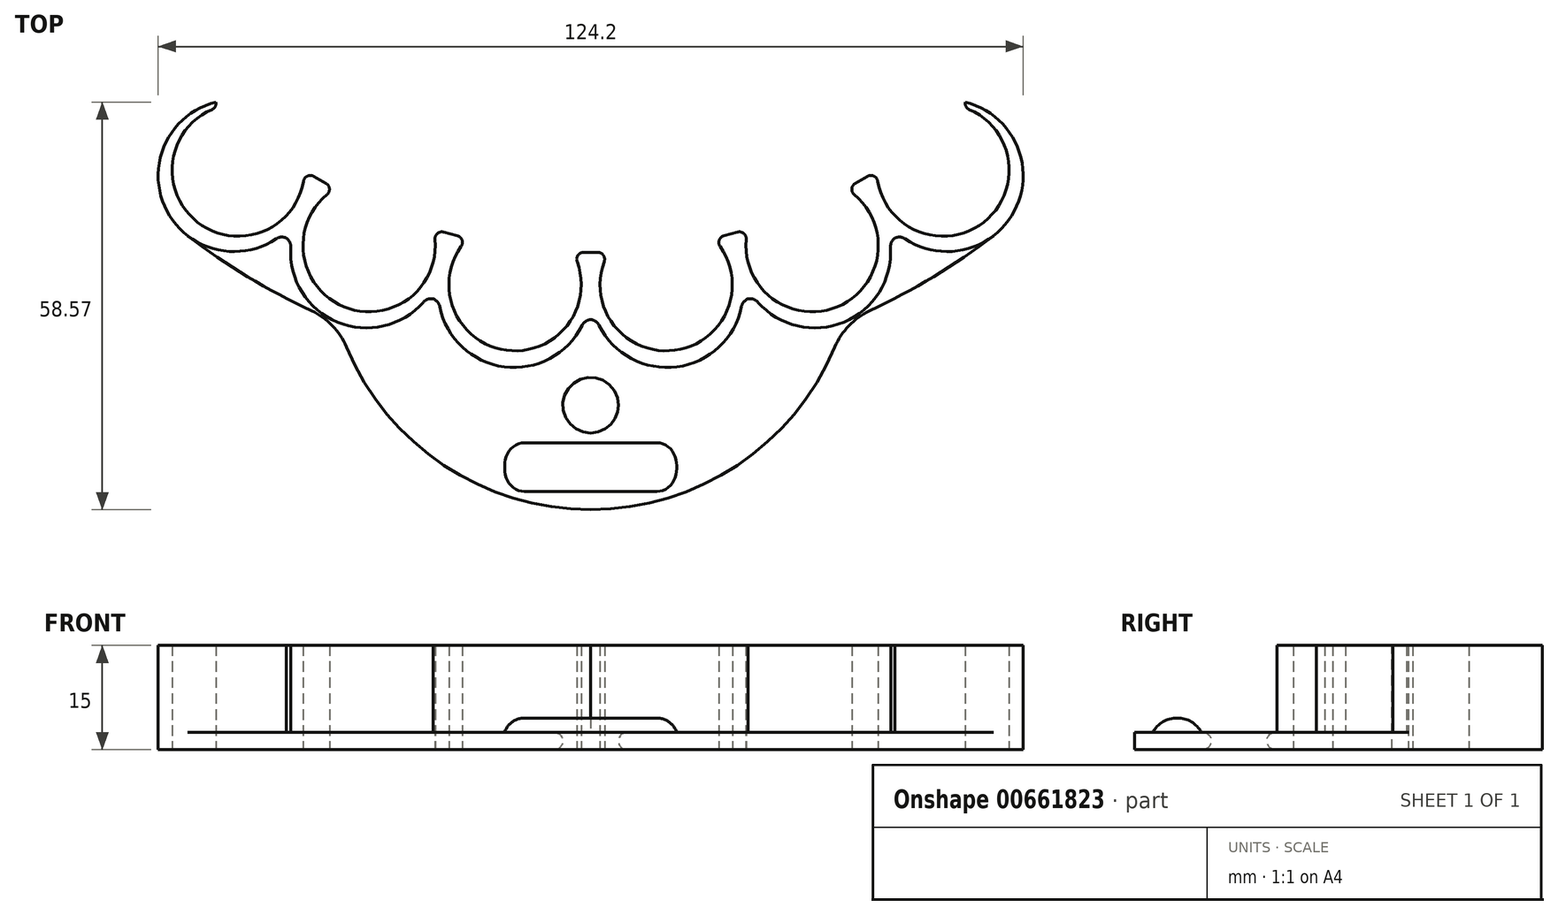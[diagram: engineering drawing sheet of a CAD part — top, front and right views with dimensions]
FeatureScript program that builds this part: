
annotation { "Feature Type Name" : "Feature", "Feature Type Description" : "" }
export const myFeature = defineFeature(function(context is Context, id is Id, definition is map)
    precondition{}
    {
        {
            assignVariable(context, id + "F0", {"name" : "clipHeight", "anyValue" : 15 * mm});
        }
        {
            var Q0;
            Q0=qCreatedBy(makeId("Top.planeOp"),FACE);
            var sketch = newSketch(context, id + "F1", { "sketchPlane" : qUnion([Q0])});
            skCircle(sketch, "E0", {"center": v(0, 0) * mm, "radius": 9.5 * mm});
            skCircle(sketch, "E1", {"center": v(0, 0) * mm, "radius": 10.3 * mm});
            skLineSegment(sketch, "E2", {"start": v(0, 0) * mm, "end": v(0, 25.39) * mm, "construction": true});
            skLineSegment(sketch, "E3", {"start": v(0, 0) * mm, "end": v(-8.5, 5.82) * mm});
            skLineSegment(sketch, "E4.MirrorCS", {"start": v(0, 0) * mm, "end": v(8.5, 5.82) * mm});
            skLineSegment(sketch, "E5", {"start": v(0, -10.3) * mm, "end": v(0, -11.9) * mm, "construction": true});
            skArc(sketch, "E6", {"start": v(-8.5, 5.82) * mm, "mid": v(0, -11.9) * mm, "end": v(8.5, 5.82) * mm});
            skLineSegment(sketch, "E7", {"start": v(0, -11.9) * mm, "end": v(0, 83.1) * mm, "construction": true});
            skLineSegment(sketch, "E8.1.0", {"start": v(24.59, -8.66) * mm, "end": v(0, 83.1) * mm, "construction": true});
            skArc(sketch, "E8.1.1", {"start": v(11.8, 6.25) * mm, "mid": v(24.59, -8.66) * mm, "end": v(28.21, 10.65) * mm});
            skCircle(sketch, "E8.1.2", {"center": v(21.5, 2.83) * mm, "radius": 10.3 * mm});
            skCircle(sketch, "E8.1.3", {"center": v(21.5, 2.83) * mm, "radius": 9.5 * mm});
            skLineSegment(sketch, "E8.1.4", {"start": v(21.5, 2.83) * mm, "end": v(14.94, 27.36) * mm, "construction": true});
            skLineSegment(sketch, "E8.1.5", {"start": v(24.17, -7.12) * mm, "end": v(24.59, -8.66) * mm, "construction": true});
            skLineSegment(sketch, "E8.1.6", {"start": v(21.5, 2.83) * mm, "end": v(28.21, 10.65) * mm});
            skLineSegment(sketch, "E8.1.7", {"start": v(21.5, 2.83) * mm, "end": v(11.8, 6.25) * mm});
            skLineSegment(sketch, "E8.2.0", {"start": v(47.5, 0.83) * mm, "end": v(0, 83.1) * mm, "construction": true});
            skArc(sketch, "E8.2.1", {"start": v(31.28, 11.92) * mm, "mid": v(47.5, 0.83) * mm, "end": v(46, 20.42) * mm});
            skCircle(sketch, "E8.2.2", {"center": v(41.55, 11.13) * mm, "radius": 10.3 * mm});
            skCircle(sketch, "E8.2.3", {"center": v(41.55, 11.13) * mm, "radius": 9.5 * mm});
            skLineSegment(sketch, "E8.2.4", {"start": v(41.55, 11.13) * mm, "end": v(28.86, 33.12) * mm, "construction": true});
            skLineSegment(sketch, "E8.2.5", {"start": v(46.7, 2.21) * mm, "end": v(47.5, 0.83) * mm, "construction": true});
            skLineSegment(sketch, "E8.2.6", {"start": v(41.55, 11.13) * mm, "end": v(46, 20.42) * mm});
            skLineSegment(sketch, "E8.2.7", {"start": v(41.55, 11.13) * mm, "end": v(31.28, 11.92) * mm});
            skLineSegment(sketch, "E8.3.0", {"start": v(67.18, 15.92) * mm, "end": v(0, 83.1) * mm, "construction": true});
            skArc(sketch, "E8.3.1", {"start": v(48.64, 22.44) * mm, "mid": v(67.18, 15.92) * mm, "end": v(60.66, 34.46) * mm});
            skCircle(sketch, "E8.3.2", {"center": v(58.76, 24.34) * mm, "radius": 10.3 * mm});
            skCircle(sketch, "E8.3.3", {"center": v(58.76, 24.34) * mm, "radius": 9.5 * mm});
            skLineSegment(sketch, "E8.3.4", {"start": v(58.76, 24.34) * mm, "end": v(40.8, 42.3) * mm, "construction": true});
            skLineSegment(sketch, "E8.3.5", {"start": v(66.04, 17.06) * mm, "end": v(67.18, 15.92) * mm, "construction": true});
            skLineSegment(sketch, "E8.3.6", {"start": v(58.76, 24.34) * mm, "end": v(60.66, 34.46) * mm});
            skLineSegment(sketch, "E8.3.7", {"start": v(58.76, 24.34) * mm, "end": v(48.64, 22.44) * mm});
            skLineSegment(sketch, "E8.4.0", {"start": v(82.27, 35.6) * mm, "end": v(0, 83.1) * mm, "construction": true});
            skArc(sketch, "E8.4.1", {"start": v(62.68, 37.1) * mm, "mid": v(82.27, 35.6) * mm, "end": v(71.18, 51.82) * mm});
            skCircle(sketch, "E8.4.2", {"center": v(71.97, 41.55) * mm, "radius": 10.3 * mm});
            skCircle(sketch, "E8.4.3", {"center": v(71.97, 41.55) * mm, "radius": 9.5 * mm});
            skLineSegment(sketch, "E8.4.4", {"start": v(71.97, 41.55) * mm, "end": v(49.98, 54.24) * mm, "construction": true});
            skLineSegment(sketch, "E8.4.5", {"start": v(80.89, 36.4) * mm, "end": v(82.27, 35.6) * mm, "construction": true});
            skLineSegment(sketch, "E8.4.6", {"start": v(71.97, 41.55) * mm, "end": v(71.18, 51.82) * mm});
            skLineSegment(sketch, "E8.4.7", {"start": v(71.97, 41.55) * mm, "end": v(62.68, 37.1) * mm});
            skLineSegment(sketch, "E8.5.0", {"start": v(91.76, 58.51) * mm, "end": v(0, 83.1) * mm, "construction": true});
            skArc(sketch, "E8.5.1", {"start": v(72.45, 54.89) * mm, "mid": v(91.76, 58.51) * mm, "end": v(76.85, 71.3) * mm});
            skCircle(sketch, "E8.5.2", {"center": v(80.27, 61.6) * mm, "radius": 10.3 * mm});
            skCircle(sketch, "E8.5.3", {"center": v(80.27, 61.6) * mm, "radius": 9.5 * mm});
            skLineSegment(sketch, "E8.5.4", {"start": v(80.27, 61.6) * mm, "end": v(55.74, 68.16) * mm, "construction": true});
            skLineSegment(sketch, "E8.5.5", {"start": v(90.22, 58.93) * mm, "end": v(91.76, 58.51) * mm, "construction": true});
            skLineSegment(sketch, "E8.5.6", {"start": v(80.27, 61.6) * mm, "end": v(76.85, 71.3) * mm});
            skLineSegment(sketch, "E8.5.7", {"start": v(80.27, 61.6) * mm, "end": v(72.45, 54.89) * mm});
            skLineSegment(sketch, "E8.6.0", {"start": v(95, 83.1) * mm, "end": v(0, 83.1) * mm, "construction": true});
            skArc(sketch, "E8.6.1", {"start": v(77.28, 74.6) * mm, "mid": v(95, 83.1) * mm, "end": v(77.28, 91.6) * mm});
            skCircle(sketch, "E8.6.2", {"center": v(83.1, 83.1) * mm, "radius": 10.3 * mm});
            skCircle(sketch, "E8.6.3", {"center": v(83.1, 83.1) * mm, "radius": 9.5 * mm});
            skLineSegment(sketch, "E8.6.4", {"start": v(83.1, 83.1) * mm, "end": v(57.71, 83.1) * mm, "construction": true});
            skLineSegment(sketch, "E8.6.5", {"start": v(93.4, 83.1) * mm, "end": v(95, 83.1) * mm, "construction": true});
            skLineSegment(sketch, "E8.6.6", {"start": v(83.1, 83.1) * mm, "end": v(77.28, 91.6) * mm});
            skLineSegment(sketch, "E8.6.7", {"start": v(83.1, 83.1) * mm, "end": v(77.28, 74.6) * mm});
            skLineSegment(sketch, "E8.7.0", {"start": v(91.76, 107.69) * mm, "end": v(0, 83.1) * mm, "construction": true});
            skArc(sketch, "E8.7.1", {"start": v(76.85, 94.9) * mm, "mid": v(91.76, 107.69) * mm, "end": v(72.45, 111.31) * mm});
            skCircle(sketch, "E8.7.2", {"center": v(80.27, 104.6) * mm, "radius": 10.3 * mm});
            skCircle(sketch, "E8.7.3", {"center": v(80.27, 104.6) * mm, "radius": 9.5 * mm});
            skLineSegment(sketch, "E8.7.4", {"start": v(80.27, 104.6) * mm, "end": v(55.74, 98.04) * mm, "construction": true});
            skLineSegment(sketch, "E8.7.5", {"start": v(90.22, 107.27) * mm, "end": v(91.76, 107.69) * mm, "construction": true});
            skLineSegment(sketch, "E8.7.6", {"start": v(80.27, 104.6) * mm, "end": v(72.45, 111.31) * mm});
            skLineSegment(sketch, "E8.7.7", {"start": v(80.27, 104.6) * mm, "end": v(76.85, 94.9) * mm});
            skLineSegment(sketch, "E8.8.0", {"start": v(82.27, 130.6) * mm, "end": v(0, 83.1) * mm, "construction": true});
            skArc(sketch, "E8.8.1", {"start": v(71.18, 114.38) * mm, "mid": v(82.27, 130.6) * mm, "end": v(62.68, 129.1) * mm});
            skCircle(sketch, "E8.8.2", {"center": v(71.97, 124.65) * mm, "radius": 10.3 * mm});
            skCircle(sketch, "E8.8.3", {"center": v(71.97, 124.65) * mm, "radius": 9.5 * mm});
            skLineSegment(sketch, "E8.8.4", {"start": v(71.97, 124.65) * mm, "end": v(49.98, 111.96) * mm, "construction": true});
            skLineSegment(sketch, "E8.8.5", {"start": v(80.89, 129.8) * mm, "end": v(82.27, 130.6) * mm, "construction": true});
            skLineSegment(sketch, "E8.8.6", {"start": v(71.97, 124.65) * mm, "end": v(62.68, 129.1) * mm});
            skLineSegment(sketch, "E8.8.7", {"start": v(71.97, 124.65) * mm, "end": v(71.18, 114.38) * mm});
            skLineSegment(sketch, "E8.9.0", {"start": v(67.18, 150.28) * mm, "end": v(0, 83.1) * mm, "construction": true});
            skArc(sketch, "E8.9.1", {"start": v(60.66, 131.74) * mm, "mid": v(67.18, 150.28) * mm, "end": v(48.64, 143.76) * mm});
            skCircle(sketch, "E8.9.2", {"center": v(58.76, 141.86) * mm, "radius": 10.3 * mm});
            skCircle(sketch, "E8.9.3", {"center": v(58.76, 141.86) * mm, "radius": 9.5 * mm});
            skLineSegment(sketch, "E8.9.4", {"start": v(58.76, 141.86) * mm, "end": v(40.8, 123.9) * mm, "construction": true});
            skLineSegment(sketch, "E8.9.5", {"start": v(66.04, 149.14) * mm, "end": v(67.18, 150.28) * mm, "construction": true});
            skLineSegment(sketch, "E8.9.6", {"start": v(58.76, 141.86) * mm, "end": v(48.64, 143.76) * mm});
            skLineSegment(sketch, "E8.9.7", {"start": v(58.76, 141.86) * mm, "end": v(60.66, 131.74) * mm});
            skLineSegment(sketch, "E8.10.0", {"start": v(47.5, 165.37) * mm, "end": v(0, 83.1) * mm, "construction": true});
            skArc(sketch, "E8.10.1", {"start": v(46, 145.78) * mm, "mid": v(47.5, 165.37) * mm, "end": v(31.28, 154.28) * mm});
            skCircle(sketch, "E8.10.2", {"center": v(41.55, 155.07) * mm, "radius": 10.3 * mm});
            skCircle(sketch, "E8.10.3", {"center": v(41.55, 155.07) * mm, "radius": 9.5 * mm});
            skLineSegment(sketch, "E8.10.4", {"start": v(41.55, 155.07) * mm, "end": v(28.86, 133.08) * mm, "construction": true});
            skLineSegment(sketch, "E8.10.5", {"start": v(46.7, 163.99) * mm, "end": v(47.5, 165.37) * mm, "construction": true});
            skLineSegment(sketch, "E8.10.6", {"start": v(41.55, 155.07) * mm, "end": v(31.28, 154.28) * mm});
            skLineSegment(sketch, "E8.10.7", {"start": v(41.55, 155.07) * mm, "end": v(46, 145.78) * mm});
            skLineSegment(sketch, "E8.11.0", {"start": v(24.59, 174.86) * mm, "end": v(0, 83.1) * mm, "construction": true});
            skArc(sketch, "E8.11.1", {"start": v(28.21, 155.55) * mm, "mid": v(24.59, 174.86) * mm, "end": v(11.8, 159.95) * mm});
            skCircle(sketch, "E8.11.2", {"center": v(21.5, 163.37) * mm, "radius": 10.3 * mm});
            skCircle(sketch, "E8.11.3", {"center": v(21.5, 163.37) * mm, "radius": 9.5 * mm});
            skLineSegment(sketch, "E8.11.4", {"start": v(21.5, 163.37) * mm, "end": v(14.94, 138.84) * mm, "construction": true});
            skLineSegment(sketch, "E8.11.5", {"start": v(24.17, 173.32) * mm, "end": v(24.59, 174.86) * mm, "construction": true});
            skLineSegment(sketch, "E8.11.6", {"start": v(21.5, 163.37) * mm, "end": v(11.8, 159.95) * mm});
            skLineSegment(sketch, "E8.11.7", {"start": v(21.5, 163.37) * mm, "end": v(28.21, 155.55) * mm});
            skLineSegment(sketch, "E8.12.0", {"start": v(0, 178.1) * mm, "end": v(0, 83.1) * mm, "construction": true});
            skArc(sketch, "E8.12.1", {"start": v(8.5, 160.38) * mm, "mid": v(0, 178.1) * mm, "end": v(-8.5, 160.38) * mm});
            skCircle(sketch, "E8.12.2", {"center": v(0, 166.2) * mm, "radius": 10.3 * mm});
            skCircle(sketch, "E8.12.3", {"center": v(0, 166.2) * mm, "radius": 9.5 * mm});
            skLineSegment(sketch, "E8.12.4", {"start": v(0, 166.2) * mm, "end": v(0, 140.81) * mm, "construction": true});
            skLineSegment(sketch, "E8.12.5", {"start": v(0, 176.5) * mm, "end": v(0, 178.1) * mm, "construction": true});
            skLineSegment(sketch, "E8.12.6", {"start": v(0, 166.2) * mm, "end": v(-8.5, 160.38) * mm});
            skLineSegment(sketch, "E8.12.7", {"start": v(0, 166.2) * mm, "end": v(8.5, 160.38) * mm});
            skLineSegment(sketch, "E8.13.0", {"start": v(-24.59, 174.86) * mm, "end": v(0, 83.1) * mm, "construction": true});
            skArc(sketch, "E8.13.1", {"start": v(-11.8, 159.95) * mm, "mid": v(-24.59, 174.86) * mm, "end": v(-28.21, 155.55) * mm});
            skCircle(sketch, "E8.13.2", {"center": v(-21.5, 163.37) * mm, "radius": 10.3 * mm});
            skCircle(sketch, "E8.13.3", {"center": v(-21.5, 163.37) * mm, "radius": 9.5 * mm});
            skLineSegment(sketch, "E8.13.4", {"start": v(-21.5, 163.37) * mm, "end": v(-14.94, 138.84) * mm, "construction": true});
            skLineSegment(sketch, "E8.13.5", {"start": v(-24.17, 173.32) * mm, "end": v(-24.59, 174.86) * mm, "construction": true});
            skLineSegment(sketch, "E8.13.6", {"start": v(-21.5, 163.37) * mm, "end": v(-28.21, 155.55) * mm});
            skLineSegment(sketch, "E8.13.7", {"start": v(-21.5, 163.37) * mm, "end": v(-11.8, 159.95) * mm});
            skLineSegment(sketch, "E8.14.0", {"start": v(-47.5, 165.37) * mm, "end": v(0, 83.1) * mm, "construction": true});
            skArc(sketch, "E8.14.1", {"start": v(-31.28, 154.28) * mm, "mid": v(-47.5, 165.37) * mm, "end": v(-46, 145.78) * mm});
            skCircle(sketch, "E8.14.2", {"center": v(-41.55, 155.07) * mm, "radius": 10.3 * mm});
            skCircle(sketch, "E8.14.3", {"center": v(-41.55, 155.07) * mm, "radius": 9.5 * mm});
            skLineSegment(sketch, "E8.14.4", {"start": v(-41.55, 155.07) * mm, "end": v(-28.86, 133.08) * mm, "construction": true});
            skLineSegment(sketch, "E8.14.5", {"start": v(-46.7, 163.99) * mm, "end": v(-47.5, 165.37) * mm, "construction": true});
            skLineSegment(sketch, "E8.14.6", {"start": v(-41.55, 155.07) * mm, "end": v(-46, 145.78) * mm});
            skLineSegment(sketch, "E8.14.7", {"start": v(-41.55, 155.07) * mm, "end": v(-31.28, 154.28) * mm});
            skLineSegment(sketch, "E8.15.0", {"start": v(-67.18, 150.28) * mm, "end": v(0, 83.1) * mm, "construction": true});
            skArc(sketch, "E8.15.1", {"start": v(-48.64, 143.76) * mm, "mid": v(-67.18, 150.28) * mm, "end": v(-60.66, 131.74) * mm});
            skCircle(sketch, "E8.15.2", {"center": v(-58.76, 141.86) * mm, "radius": 10.3 * mm});
            skCircle(sketch, "E8.15.3", {"center": v(-58.76, 141.86) * mm, "radius": 9.5 * mm});
            skLineSegment(sketch, "E8.15.4", {"start": v(-58.76, 141.86) * mm, "end": v(-40.8, 123.9) * mm, "construction": true});
            skLineSegment(sketch, "E8.15.5", {"start": v(-66.04, 149.14) * mm, "end": v(-67.18, 150.28) * mm, "construction": true});
            skLineSegment(sketch, "E8.15.6", {"start": v(-58.76, 141.86) * mm, "end": v(-60.66, 131.74) * mm});
            skLineSegment(sketch, "E8.15.7", {"start": v(-58.76, 141.86) * mm, "end": v(-48.64, 143.76) * mm});
            skLineSegment(sketch, "E8.16.0", {"start": v(-82.27, 130.6) * mm, "end": v(0, 83.1) * mm, "construction": true});
            skArc(sketch, "E8.16.1", {"start": v(-62.68, 129.1) * mm, "mid": v(-82.27, 130.6) * mm, "end": v(-71.18, 114.38) * mm});
            skCircle(sketch, "E8.16.2", {"center": v(-71.97, 124.65) * mm, "radius": 10.3 * mm});
            skCircle(sketch, "E8.16.3", {"center": v(-71.97, 124.65) * mm, "radius": 9.5 * mm});
            skLineSegment(sketch, "E8.16.4", {"start": v(-71.97, 124.65) * mm, "end": v(-49.98, 111.96) * mm, "construction": true});
            skLineSegment(sketch, "E8.16.5", {"start": v(-80.89, 129.8) * mm, "end": v(-82.27, 130.6) * mm, "construction": true});
            skLineSegment(sketch, "E8.16.6", {"start": v(-71.97, 124.65) * mm, "end": v(-71.18, 114.38) * mm});
            skLineSegment(sketch, "E8.16.7", {"start": v(-71.97, 124.65) * mm, "end": v(-62.68, 129.1) * mm});
            skLineSegment(sketch, "E8.17.0", {"start": v(-91.76, 107.69) * mm, "end": v(0, 83.1) * mm, "construction": true});
            skArc(sketch, "E8.17.1", {"start": v(-72.45, 111.31) * mm, "mid": v(-91.76, 107.69) * mm, "end": v(-76.85, 94.9) * mm});
            skCircle(sketch, "E8.17.2", {"center": v(-80.27, 104.6) * mm, "radius": 10.3 * mm});
            skCircle(sketch, "E8.17.3", {"center": v(-80.27, 104.6) * mm, "radius": 9.5 * mm});
            skLineSegment(sketch, "E8.17.4", {"start": v(-80.27, 104.6) * mm, "end": v(-55.74, 98.04) * mm, "construction": true});
            skLineSegment(sketch, "E8.17.5", {"start": v(-90.22, 107.27) * mm, "end": v(-91.76, 107.69) * mm, "construction": true});
            skLineSegment(sketch, "E8.17.6", {"start": v(-80.27, 104.6) * mm, "end": v(-76.85, 94.9) * mm});
            skLineSegment(sketch, "E8.17.7", {"start": v(-80.27, 104.6) * mm, "end": v(-72.45, 111.31) * mm});
            skLineSegment(sketch, "E8.18.0", {"start": v(-95, 83.1) * mm, "end": v(0, 83.1) * mm, "construction": true});
            skArc(sketch, "E8.18.1", {"start": v(-77.28, 91.6) * mm, "mid": v(-95, 83.1) * mm, "end": v(-77.28, 74.6) * mm});
            skCircle(sketch, "E8.18.2", {"center": v(-83.1, 83.1) * mm, "radius": 10.3 * mm});
            skCircle(sketch, "E8.18.3", {"center": v(-83.1, 83.1) * mm, "radius": 9.5 * mm});
            skLineSegment(sketch, "E8.18.4", {"start": v(-83.1, 83.1) * mm, "end": v(-57.71, 83.1) * mm, "construction": true});
            skLineSegment(sketch, "E8.18.5", {"start": v(-93.4, 83.1) * mm, "end": v(-95, 83.1) * mm, "construction": true});
            skLineSegment(sketch, "E8.18.6", {"start": v(-83.1, 83.1) * mm, "end": v(-77.28, 74.6) * mm});
            skLineSegment(sketch, "E8.18.7", {"start": v(-83.1, 83.1) * mm, "end": v(-77.28, 91.6) * mm});
            skLineSegment(sketch, "E8.19.0", {"start": v(-91.76, 58.51) * mm, "end": v(0, 83.1) * mm, "construction": true});
            skArc(sketch, "E8.19.1", {"start": v(-76.85, 71.3) * mm, "mid": v(-91.76, 58.51) * mm, "end": v(-72.45, 54.89) * mm});
            skCircle(sketch, "E8.19.2", {"center": v(-80.27, 61.6) * mm, "radius": 10.3 * mm});
            skCircle(sketch, "E8.19.3", {"center": v(-80.27, 61.6) * mm, "radius": 9.5 * mm});
            skLineSegment(sketch, "E8.19.4", {"start": v(-80.27, 61.6) * mm, "end": v(-55.74, 68.16) * mm, "construction": true});
            skLineSegment(sketch, "E8.19.5", {"start": v(-90.22, 58.93) * mm, "end": v(-91.76, 58.51) * mm, "construction": true});
            skLineSegment(sketch, "E8.19.6", {"start": v(-80.27, 61.6) * mm, "end": v(-72.45, 54.89) * mm});
            skLineSegment(sketch, "E8.19.7", {"start": v(-80.27, 61.6) * mm, "end": v(-76.85, 71.3) * mm});
            skLineSegment(sketch, "E8.20.0", {"start": v(-82.27, 35.6) * mm, "end": v(0, 83.1) * mm, "construction": true});
            skArc(sketch, "E8.20.1", {"start": v(-71.18, 51.82) * mm, "mid": v(-82.27, 35.6) * mm, "end": v(-62.68, 37.1) * mm});
            skCircle(sketch, "E8.20.2", {"center": v(-71.97, 41.55) * mm, "radius": 10.3 * mm});
            skCircle(sketch, "E8.20.3", {"center": v(-71.97, 41.55) * mm, "radius": 9.5 * mm});
            skLineSegment(sketch, "E8.20.4", {"start": v(-71.97, 41.55) * mm, "end": v(-49.98, 54.24) * mm, "construction": true});
            skLineSegment(sketch, "E8.20.5", {"start": v(-80.89, 36.4) * mm, "end": v(-82.27, 35.6) * mm, "construction": true});
            skLineSegment(sketch, "E8.20.6", {"start": v(-71.97, 41.55) * mm, "end": v(-62.68, 37.1) * mm});
            skLineSegment(sketch, "E8.20.7", {"start": v(-71.97, 41.55) * mm, "end": v(-71.18, 51.82) * mm});
            skLineSegment(sketch, "E8.21.0", {"start": v(-67.18, 15.92) * mm, "end": v(0, 83.1) * mm, "construction": true});
            skArc(sketch, "E8.21.1", {"start": v(-60.66, 34.46) * mm, "mid": v(-67.18, 15.92) * mm, "end": v(-48.64, 22.44) * mm});
            skCircle(sketch, "E8.21.2", {"center": v(-58.76, 24.34) * mm, "radius": 10.3 * mm});
            skCircle(sketch, "E8.21.3", {"center": v(-58.76, 24.34) * mm, "radius": 9.5 * mm});
            skLineSegment(sketch, "E8.21.4", {"start": v(-58.76, 24.34) * mm, "end": v(-40.8, 42.3) * mm, "construction": true});
            skLineSegment(sketch, "E8.21.5", {"start": v(-66.04, 17.06) * mm, "end": v(-67.18, 15.92) * mm, "construction": true});
            skLineSegment(sketch, "E8.21.6", {"start": v(-58.76, 24.34) * mm, "end": v(-48.64, 22.44) * mm});
            skLineSegment(sketch, "E8.21.7", {"start": v(-58.76, 24.34) * mm, "end": v(-60.66, 34.46) * mm});
            skLineSegment(sketch, "E8.22.0", {"start": v(-47.5, 0.83) * mm, "end": v(0, 83.1) * mm, "construction": true});
            skArc(sketch, "E8.22.1", {"start": v(-46, 20.42) * mm, "mid": v(-47.5, 0.83) * mm, "end": v(-31.28, 11.92) * mm});
            skCircle(sketch, "E8.22.2", {"center": v(-41.55, 11.13) * mm, "radius": 10.3 * mm});
            skCircle(sketch, "E8.22.3", {"center": v(-41.55, 11.13) * mm, "radius": 9.5 * mm});
            skLineSegment(sketch, "E8.22.4", {"start": v(-41.55, 11.13) * mm, "end": v(-28.86, 33.12) * mm, "construction": true});
            skLineSegment(sketch, "E8.22.5", {"start": v(-46.7, 2.21) * mm, "end": v(-47.5, 0.83) * mm, "construction": true});
            skLineSegment(sketch, "E8.22.6", {"start": v(-41.55, 11.13) * mm, "end": v(-31.28, 11.92) * mm});
            skLineSegment(sketch, "E8.22.7", {"start": v(-41.55, 11.13) * mm, "end": v(-46, 20.42) * mm});
            skLineSegment(sketch, "E8.23.0", {"start": v(-24.59, -8.66) * mm, "end": v(0, 83.1) * mm, "construction": true});
            skArc(sketch, "E8.23.1", {"start": v(-28.21, 10.65) * mm, "mid": v(-24.59, -8.66) * mm, "end": v(-11.8, 6.25) * mm});
            skCircle(sketch, "E8.23.2", {"center": v(-21.5, 2.83) * mm, "radius": 10.3 * mm});
            skCircle(sketch, "E8.23.3", {"center": v(-21.5, 2.83) * mm, "radius": 9.5 * mm});
            skLineSegment(sketch, "E8.23.4", {"start": v(-21.5, 2.83) * mm, "end": v(-14.94, 27.36) * mm, "construction": true});
            skLineSegment(sketch, "E8.23.5", {"start": v(-24.17, -7.12) * mm, "end": v(-24.59, -8.66) * mm, "construction": true});
            skLineSegment(sketch, "E8.23.6", {"start": v(-21.5, 2.83) * mm, "end": v(-11.8, 6.25) * mm});
            skLineSegment(sketch, "E8.23.7", {"start": v(-21.5, 2.83) * mm, "end": v(-28.21, 10.65) * mm});
            skPoint(sketch, "E8.center", {"position": v(0, 83.1) * mm});
            skArc(sketch, "E9", {"start": v(0, -11.9) * mm, "mid": v(57.83, 7.73) * mm, "end": v(91.76, 58.51) * mm});
            skArc(sketch, "E10", {"start": v(24.59, -8.66) * mm, "mid": v(69.83, -7.9) * mm, "end": v(82.27, 35.6) * mm});
            skLineSegment(sketch, "E11", {"start": v(0, -1) * mm, "end": v(21.77, 1.86) * mm});
            skLineSegment(sketch, "E12", {"start": v(21.77, 1.86) * mm, "end": v(42.05, 10.27) * mm});
            skLineSegment(sketch, "E13", {"start": v(42.05, 10.27) * mm, "end": v(59.47, 23.63) * mm});
            skLineSegment(sketch, "E14", {"start": v(59.47, 23.63) * mm, "end": v(72.83, 41.05) * mm});
            skLineSegment(sketch, "E15", {"start": v(81.24, 61.33) * mm, "end": v(72.83, 41.05) * mm});
            skLineSegment(sketch, "E16", {"start": v(69.83, -7.9) * mm, "end": v(57.83, 7.73) * mm, "construction": true});
            skCircle(sketch, "E17", {"center": v(60.7, 4) * mm, "radius": 4 * mm});
            skLineSegment(sketch, "E18", {"start": v(81.43, 51.36) * mm, "end": v(80.03, 47.96) * mm});
            skLineSegment(sketch, "E19", {"start": v(70.44, 31.36) * mm, "end": v(68.2, 28.45) * mm});
            skLineSegment(sketch, "E20", {"start": v(54.65, 14.9) * mm, "end": v(51.74, 12.66) * mm});
            skLineSegment(sketch, "E21", {"start": v(35.14, 3.07) * mm, "end": v(31.74, 1.67) * mm});
            skLineSegment(sketch, "E22", {"start": v(13.23, -3.3) * mm, "end": v(9.58, -3.78) * mm});
            skLineSegment(sketch, "E23", {"start": v(72.45, 54.89) * mm, "end": v(71.18, 51.82) * mm});
            skLineSegment(sketch, "E24", {"start": v(62.68, 37.1) * mm, "end": v(60.66, 34.46) * mm});
            skLineSegment(sketch, "E25", {"start": v(48.64, 22.44) * mm, "end": v(46, 20.42) * mm});
            skLineSegment(sketch, "E26", {"start": v(31.28, 11.92) * mm, "end": v(28.21, 10.65) * mm});
            skLineSegment(sketch, "E27", {"start": v(11.8, 6.25) * mm, "end": v(8.5, 5.82) * mm});
            skSolve(sketch);
        }
        {
            var Q0;
            {var subQ0=sQuery(id+"F1.wireOp",EDGE,"E3");var subQ1=sQuery(id+"F1.wireOp",EDGE,"E0");var subQ2=makeQuery(id+"F1.imprint","INTERSECT",VERTEX,{"derivedFrom":[subQ1,subQ0]});Q0=makeQuery(id+"F1.imprint","IMPRINT",FACE,{"disambiguationData":[TD([[makeQuery(id+"F1.imprint","IMPRINT",EDGE,{"disambiguationData":[TD([[subQ2,-1.0]])],"derivedFrom":subQ1}),-1.0]])]});}
            var Q1;
            {var subQ0=sQuery(id+"F1.wireOp",EDGE,"E6");Q1=makeQuery(id+"F1.imprint","IMPRINT",FACE,{"disambiguationData":[TD([[makeQuery(id+"F1.imprint","IMPRINT",EDGE,{"derivedFrom":subQ0}),1.0]])]});}
            var Q2;
            {var subQ0=sQuery(id+"F1.wireOp",EDGE,"E8.1.1");Q2=makeQuery(id+"F1.imprint","IMPRINT",FACE,{"disambiguationData":[TD([[makeQuery(id+"F1.imprint","IMPRINT",EDGE,{"derivedFrom":subQ0}),1.0]])]});}
            var Q3;
            {var subQ4=sQuery(id+"F1.wireOp",EDGE,"E8.1.6");var subQ6=sQuery(id+"F1.wireOp",EDGE,"E8.1.3");var subQ7=makeQuery(id+"F1.imprint","INTERSECT",VERTEX,{"derivedFrom":[subQ6,subQ4]});Q3=makeQuery(id+"F1.imprint","IMPRINT",FACE,{"disambiguationData":[TD([[makeQuery(id+"F1.imprint","IMPRINT",EDGE,{"disambiguationData":[TD([[subQ7,1.0]])],"derivedFrom":subQ6}),-1.0]])]});}
            var Q4;
            {var subQ4=sQuery(id+"F1.wireOp",EDGE,"E8.2.6");var subQ6=sQuery(id+"F1.wireOp",EDGE,"E8.2.3");var subQ7=makeQuery(id+"F1.imprint","INTERSECT",VERTEX,{"derivedFrom":[subQ6,subQ4]});Q4=makeQuery(id+"F1.imprint","IMPRINT",FACE,{"disambiguationData":[TD([[makeQuery(id+"F1.imprint","IMPRINT",EDGE,{"disambiguationData":[TD([[subQ7,1.0]])],"derivedFrom":subQ6}),-1.0]])]});}
            var Q5;
            {var subQ0=sQuery(id+"F1.wireOp",EDGE,"E8.2.1");Q5=makeQuery(id+"F1.imprint","IMPRINT",FACE,{"disambiguationData":[TD([[makeQuery(id+"F1.imprint","IMPRINT",EDGE,{"derivedFrom":subQ0}),1.0]])]});}
            var Q6;
            {var subQ4=sQuery(id+"F1.wireOp",EDGE,"E8.3.6");var subQ6=sQuery(id+"F1.wireOp",EDGE,"E8.3.3");var subQ7=makeQuery(id+"F1.imprint","INTERSECT",VERTEX,{"derivedFrom":[subQ6,subQ4]});Q6=makeQuery(id+"F1.imprint","IMPRINT",FACE,{"disambiguationData":[TD([[makeQuery(id+"F1.imprint","IMPRINT",EDGE,{"disambiguationData":[TD([[subQ7,1.0]])],"derivedFrom":subQ6}),-1.0]])]});}
            var Q7;
            {var subQ0=sQuery(id+"F1.wireOp",EDGE,"E8.3.1");Q7=makeQuery(id+"F1.imprint","IMPRINT",FACE,{"disambiguationData":[TD([[makeQuery(id+"F1.imprint","IMPRINT",EDGE,{"derivedFrom":subQ0}),1.0]])]});}
            var Q8;
            {var subQ0=sQuery(id+"F1.wireOp",EDGE,"E8.4.1");Q8=makeQuery(id+"F1.imprint","IMPRINT",FACE,{"disambiguationData":[TD([[makeQuery(id+"F1.imprint","IMPRINT",EDGE,{"derivedFrom":subQ0}),1.0]])]});}
            var Q9;
            {var subQ4=sQuery(id+"F1.wireOp",EDGE,"E8.5.6");var subQ6=sQuery(id+"F1.wireOp",EDGE,"E8.5.3");var subQ7=makeQuery(id+"F1.imprint","INTERSECT",VERTEX,{"derivedFrom":[subQ6,subQ4]});Q9=makeQuery(id+"F1.imprint","IMPRINT",FACE,{"disambiguationData":[TD([[makeQuery(id+"F1.imprint","IMPRINT",EDGE,{"disambiguationData":[TD([[subQ7,1.0]])],"derivedFrom":subQ6}),-1.0]])]});}
            var Q10;
            {var subQ0=sQuery(id+"F1.wireOp",EDGE,"E8.5.1");Q10=makeQuery(id+"F1.imprint","IMPRINT",FACE,{"disambiguationData":[TD([[makeQuery(id+"F1.imprint","IMPRINT",EDGE,{"derivedFrom":subQ0}),1.0]])]});}
            var Q11;
            {var subQ0=sQuery(id+"F1.wireOp",EDGE,"E14");var subQ1=sQuery(id+"F1.wireOp",EDGE,"E8.3.2");var subQ2=makeQuery(id+"F1.imprint","INTERSECT",VERTEX,{"derivedFrom":[subQ1,subQ0]});Q11=makeQuery(id+"F1.imprint","IMPRINT",FACE,{"disambiguationData":[TD([[makeQuery(id+"F1.imprint","IMPRINT",EDGE,{"disambiguationData":[TD([[subQ2,1.0]])],"derivedFrom":subQ1}),1.0]])]});}
            var Q12;
            {var subQ1=sQuery(id+"F1.wireOp",EDGE,"E8.4.1");var subQ3=sQuery(id+"F1.wireOp",EDGE,"E14");var subQ4=makeQuery(id+"F1.imprint","INTERSECT",VERTEX,{"derivedFrom":[subQ1,subQ3]});Q12=makeQuery(id+"F1.imprint","IMPRINT",FACE,{"disambiguationData":[TD([[makeQuery(id+"F1.imprint","IMPRINT",EDGE,{"disambiguationData":[TD([[subQ4,-1.0]])],"derivedFrom":subQ3}),1.0]])]});}
            var Q13;
            {var subQ3=sQuery(id+"F1.wireOp",EDGE,"E14");var subQ5=sQuery(id+"F1.wireOp",EDGE,"E8.4.3");var subQ6=makeQuery(id+"F1.imprint","INTERSECT",VERTEX,{"derivedFrom":[subQ5,subQ3]});Q13=makeQuery(id+"F1.imprint","IMPRINT",FACE,{"disambiguationData":[TD([[makeQuery(id+"F1.imprint","IMPRINT",EDGE,{"disambiguationData":[TD([[subQ6,1.0]])],"derivedFrom":subQ5}),-1.0]])]});}
            var Q14;
            {var subQ0=sQuery(id+"F1.wireOp",EDGE,"E12");var subQ1=sQuery(id+"F1.wireOp",EDGE,"E8.1.2");var subQ2=makeQuery(id+"F1.imprint","INTERSECT",VERTEX,{"derivedFrom":[subQ1,subQ0]});Q14=makeQuery(id+"F1.imprint","IMPRINT",FACE,{"disambiguationData":[TD([[makeQuery(id+"F1.imprint","IMPRINT",EDGE,{"disambiguationData":[TD([[subQ2,1.0]])],"derivedFrom":subQ1}),1.0]])]});}
            var Q15;
            {var subQ0=sQuery(id+"F1.wireOp",EDGE,"E8.2.7");var subQ5=sQuery(id+"F1.wireOp",EDGE,"E8.2.3");var subQ6=makeQuery(id+"F1.imprint","INTERSECT",VERTEX,{"derivedFrom":[subQ5,subQ0]});Q15=makeQuery(id+"F1.imprint","IMPRINT",FACE,{"disambiguationData":[TD([[makeQuery(id+"F1.imprint","IMPRINT",EDGE,{"disambiguationData":[TD([[subQ6,-1.0]])],"derivedFrom":subQ5}),-1.0]])]});}
            var Q16;
            {var subQ0=sQuery(id+"F1.wireOp",EDGE,"E13");var subQ1=sQuery(id+"F1.wireOp",EDGE,"E8.2.2");var subQ2=makeQuery(id+"F1.imprint","INTERSECT",VERTEX,{"derivedFrom":[subQ1,subQ0]});Q16=makeQuery(id+"F1.imprint","IMPRINT",FACE,{"disambiguationData":[TD([[makeQuery(id+"F1.imprint","IMPRINT",EDGE,{"disambiguationData":[TD([[subQ2,1.0]])],"derivedFrom":subQ1}),1.0]])]});}
            var Q17;
            {var subQ0=sQuery(id+"F1.wireOp",EDGE,"E11");var subQ1=sQuery(id+"F1.wireOp",EDGE,"E0");var subQ2=makeQuery(id+"F1.imprint","INTERSECT",VERTEX,{"derivedFrom":[subQ1,subQ0]});Q17=makeQuery(id+"F1.imprint","IMPRINT",FACE,{"disambiguationData":[TD([[makeQuery(id+"F1.imprint","IMPRINT",EDGE,{"disambiguationData":[TD([[subQ2,-1.0]])],"derivedFrom":subQ1}),-1.0]])]});}
            var Q18;
            {var subQ0=sQuery(id+"F1.wireOp",EDGE,"E6");var subQ3=sQuery(id+"F1.wireOp",EDGE,"E11");var subQ5=makeQuery(id+"F1.imprint","INTERSECT",VERTEX,{"derivedFrom":[subQ0,subQ3]});Q18=makeQuery(id+"F1.imprint","IMPRINT",FACE,{"disambiguationData":[TD([[makeQuery(id+"F1.imprint","IMPRINT",EDGE,{"disambiguationData":[TD([[subQ5,1.0]])],"derivedFrom":subQ3}),1.0]])]});}
            var Q19;
            {var subQ1=sQuery(id+"F1.wireOp",EDGE,"E8.1.1");var subQ3=sQuery(id+"F1.wireOp",EDGE,"E11");var subQ4=makeQuery(id+"F1.imprint","INTERSECT",VERTEX,{"derivedFrom":[subQ1,subQ3]});Q19=makeQuery(id+"F1.imprint","IMPRINT",FACE,{"disambiguationData":[TD([[makeQuery(id+"F1.imprint","IMPRINT",EDGE,{"disambiguationData":[TD([[subQ4,-1.0]])],"derivedFrom":subQ3}),1.0]])]});}
            var Q20;
            {var subQ0=sQuery(id+"F1.wireOp",EDGE,"E8.1.7");var subQ5=sQuery(id+"F1.wireOp",EDGE,"E8.1.3");var subQ6=makeQuery(id+"F1.imprint","INTERSECT",VERTEX,{"derivedFrom":[subQ5,subQ0]});Q20=makeQuery(id+"F1.imprint","IMPRINT",FACE,{"disambiguationData":[TD([[makeQuery(id+"F1.imprint","IMPRINT",EDGE,{"disambiguationData":[TD([[subQ6,-1.0]])],"derivedFrom":subQ5}),-1.0]])]});}
            var Q21;
            {var subQ1=sQuery(id+"F1.wireOp",EDGE,"E8.2.1");var subQ3=sQuery(id+"F1.wireOp",EDGE,"E12");var subQ4=makeQuery(id+"F1.imprint","INTERSECT",VERTEX,{"derivedFrom":[subQ1,subQ3]});Q21=makeQuery(id+"F1.imprint","IMPRINT",FACE,{"disambiguationData":[TD([[makeQuery(id+"F1.imprint","IMPRINT",EDGE,{"disambiguationData":[TD([[subQ4,-1.0]])],"derivedFrom":subQ3}),1.0]])]});}
            var Q22;
            {var subQ1=sQuery(id+"F1.wireOp",EDGE,"E8.1.1");var subQ3=sQuery(id+"F1.wireOp",EDGE,"E12");var subQ4=makeQuery(id+"F1.imprint","INTERSECT",VERTEX,{"derivedFrom":[subQ1,subQ3]});Q22=makeQuery(id+"F1.imprint","IMPRINT",FACE,{"disambiguationData":[TD([[makeQuery(id+"F1.imprint","IMPRINT",EDGE,{"disambiguationData":[TD([[subQ4,1.0]])],"derivedFrom":subQ3}),1.0]])]});}
            var Q23;
            {var subQ0=sQuery(id+"F1.wireOp",EDGE,"E8.3.7");var subQ5=sQuery(id+"F1.wireOp",EDGE,"E8.3.3");var subQ6=makeQuery(id+"F1.imprint","INTERSECT",VERTEX,{"derivedFrom":[subQ5,subQ0]});Q23=makeQuery(id+"F1.imprint","IMPRINT",FACE,{"disambiguationData":[TD([[makeQuery(id+"F1.imprint","IMPRINT",EDGE,{"disambiguationData":[TD([[subQ6,-1.0]])],"derivedFrom":subQ5}),-1.0]])]});}
            var Q24;
            {var subQ1=sQuery(id+"F1.wireOp",EDGE,"E8.3.1");var subQ3=sQuery(id+"F1.wireOp",EDGE,"E13");var subQ4=makeQuery(id+"F1.imprint","INTERSECT",VERTEX,{"derivedFrom":[subQ1,subQ3]});Q24=makeQuery(id+"F1.imprint","IMPRINT",FACE,{"disambiguationData":[TD([[makeQuery(id+"F1.imprint","IMPRINT",EDGE,{"disambiguationData":[TD([[subQ4,-1.0]])],"derivedFrom":subQ3}),1.0]])]});}
            var Q25;
            {var subQ1=sQuery(id+"F1.wireOp",EDGE,"E8.2.1");var subQ3=sQuery(id+"F1.wireOp",EDGE,"E13");var subQ4=makeQuery(id+"F1.imprint","INTERSECT",VERTEX,{"derivedFrom":[subQ1,subQ3]});Q25=makeQuery(id+"F1.imprint","IMPRINT",FACE,{"disambiguationData":[TD([[makeQuery(id+"F1.imprint","IMPRINT",EDGE,{"disambiguationData":[TD([[subQ4,1.0]])],"derivedFrom":subQ3}),1.0]])]});}
            var Q26;
            {var subQ1=sQuery(id+"F1.wireOp",EDGE,"E8.3.1");var subQ3=sQuery(id+"F1.wireOp",EDGE,"E14");var subQ4=makeQuery(id+"F1.imprint","INTERSECT",VERTEX,{"derivedFrom":[subQ1,subQ3]});Q26=makeQuery(id+"F1.imprint","IMPRINT",FACE,{"disambiguationData":[TD([[makeQuery(id+"F1.imprint","IMPRINT",EDGE,{"disambiguationData":[TD([[subQ4,1.0]])],"derivedFrom":subQ3}),1.0]])]});}
            var Q27;
            {var subQ0=sQuery(id+"F1.wireOp",EDGE,"E15");var subQ1=sQuery(id+"F1.wireOp",EDGE,"E8.4.2");var subQ2=makeQuery(id+"F1.imprint","INTERSECT",VERTEX,{"derivedFrom":[subQ1,subQ0]});Q27=makeQuery(id+"F1.imprint","IMPRINT",FACE,{"disambiguationData":[TD([[makeQuery(id+"F1.imprint","IMPRINT",EDGE,{"disambiguationData":[TD([[subQ2,1.0]])],"derivedFrom":subQ1}),1.0]])]});}
            var Q28;
            {var subQ3=sQuery(id+"F1.wireOp",EDGE,"E15");var subQ5=sQuery(id+"F1.wireOp",EDGE,"E8.5.3");var subQ6=makeQuery(id+"F1.imprint","INTERSECT",VERTEX,{"derivedFrom":[subQ5,subQ3]});Q28=makeQuery(id+"F1.imprint","IMPRINT",FACE,{"disambiguationData":[TD([[makeQuery(id+"F1.imprint","IMPRINT",EDGE,{"disambiguationData":[TD([[subQ6,1.0]])],"derivedFrom":subQ5}),-1.0]])]});}
            var Q29;
            {var subQ1=sQuery(id+"F1.wireOp",EDGE,"E8.5.1");var subQ3=sQuery(id+"F1.wireOp",EDGE,"E15");var subQ4=makeQuery(id+"F1.imprint","INTERSECT",VERTEX,{"derivedFrom":[subQ1,subQ3]});Q29=makeQuery(id+"F1.imprint","IMPRINT",FACE,{"disambiguationData":[TD([[makeQuery(id+"F1.imprint","IMPRINT",EDGE,{"disambiguationData":[TD([[subQ4,1.0]])],"derivedFrom":subQ3}),-1.0]])]});}
            var Q30;
            {var subQ1=sQuery(id+"F1.wireOp",EDGE,"E8.4.1");var subQ3=sQuery(id+"F1.wireOp",EDGE,"E15");var subQ4=makeQuery(id+"F1.imprint","INTERSECT",VERTEX,{"derivedFrom":[subQ1,subQ3]});Q30=makeQuery(id+"F1.imprint","IMPRINT",FACE,{"disambiguationData":[TD([[makeQuery(id+"F1.imprint","IMPRINT",EDGE,{"disambiguationData":[TD([[subQ4,-1.0]])],"derivedFrom":subQ3}),-1.0]])]});}
            var Q31;
            {var subQ0=sQuery(id+"F1.wireOp",EDGE,"E8.4.6");var subQ5=sQuery(id+"F1.wireOp",EDGE,"E8.4.3");var subQ6=makeQuery(id+"F1.imprint","INTERSECT",VERTEX,{"derivedFrom":[subQ5,subQ0]});Q31=makeQuery(id+"F1.imprint","IMPRINT",FACE,{"disambiguationData":[TD([[makeQuery(id+"F1.imprint","IMPRINT",EDGE,{"disambiguationData":[TD([[subQ6,1.0]])],"derivedFrom":subQ5}),-1.0]])]});}
            var Q32;
            {var subQ0=sQuery(id+"F1.wireOp",EDGE,"E22");var subQ1=sQuery(id+"F1.wireOp",EDGE,"E1");var subQ2=makeQuery(id+"F1.imprint","INTERSECT",VERTEX,{"derivedFrom":[subQ1,subQ0]});Q32=makeQuery(id+"F1.imprint","IMPRINT",FACE,{"disambiguationData":[TD([[makeQuery(id+"F1.imprint","IMPRINT",EDGE,{"disambiguationData":[TD([[subQ2,-1.0]])],"derivedFrom":subQ1}),-1.0]])]});}
            var Q33;
            {var subQ0=sQuery(id+"F1.wireOp",EDGE,"E11");var subQ1=sQuery(id+"F1.wireOp",EDGE,"E8.1.1");var subQ2=makeQuery(id+"F1.imprint","INTERSECT",VERTEX,{"derivedFrom":[subQ1,subQ0]});Q33=makeQuery(id+"F1.imprint","IMPRINT",FACE,{"disambiguationData":[TD([[makeQuery(id+"F1.imprint","IMPRINT",EDGE,{"disambiguationData":[TD([[subQ2,-1.0]])],"derivedFrom":subQ1}),1.0]])]});}
            var Q34;
            {var subQ0=sQuery(id+"F1.wireOp",EDGE,"E11");var subQ1=sQuery(id+"F1.wireOp",EDGE,"E6");var subQ2=makeQuery(id+"F1.imprint","INTERSECT",VERTEX,{"derivedFrom":[subQ1,subQ0]});Q34=makeQuery(id+"F1.imprint","IMPRINT",FACE,{"disambiguationData":[TD([[makeQuery(id+"F1.imprint","IMPRINT",EDGE,{"disambiguationData":[TD([[subQ2,1.0]])],"derivedFrom":subQ1}),-1.0]])]});}
            var Q35;
            {var subQ0=sQuery(id+"F1.wireOp",EDGE,"E12");var subQ1=sQuery(id+"F1.wireOp",EDGE,"E8.2.1");var subQ2=makeQuery(id+"F1.imprint","INTERSECT",VERTEX,{"derivedFrom":[subQ1,subQ0]});Q35=makeQuery(id+"F1.imprint","IMPRINT",FACE,{"disambiguationData":[TD([[makeQuery(id+"F1.imprint","IMPRINT",EDGE,{"disambiguationData":[TD([[subQ2,-1.0]])],"derivedFrom":subQ1}),1.0]])]});}
            var Q36;
            {var subQ0=sQuery(id+"F1.wireOp",EDGE,"E12");var subQ1=sQuery(id+"F1.wireOp",EDGE,"E8.1.1");var subQ2=makeQuery(id+"F1.imprint","INTERSECT",VERTEX,{"derivedFrom":[subQ1,subQ0]});Q36=makeQuery(id+"F1.imprint","IMPRINT",FACE,{"disambiguationData":[TD([[makeQuery(id+"F1.imprint","IMPRINT",EDGE,{"disambiguationData":[TD([[subQ2,1.0]])],"derivedFrom":subQ1}),-1.0]])]});}
            var Q37;
            {var subQ0=sQuery(id+"F1.wireOp",EDGE,"E12");var subQ1=sQuery(id+"F1.wireOp",EDGE,"E8.1.1");var subQ2=makeQuery(id+"F1.imprint","INTERSECT",VERTEX,{"derivedFrom":[subQ1,subQ0]});Q37=makeQuery(id+"F1.imprint","IMPRINT",FACE,{"disambiguationData":[TD([[makeQuery(id+"F1.imprint","IMPRINT",EDGE,{"disambiguationData":[TD([[subQ2,1.0]])],"derivedFrom":subQ1}),1.0]])]});}
            var Q38;
            {var subQ0=sQuery(id+"F1.wireOp",EDGE,"E13");var subQ1=sQuery(id+"F1.wireOp",EDGE,"E8.2.1");var subQ2=makeQuery(id+"F1.imprint","INTERSECT",VERTEX,{"derivedFrom":[subQ1,subQ0]});Q38=makeQuery(id+"F1.imprint","IMPRINT",FACE,{"disambiguationData":[TD([[makeQuery(id+"F1.imprint","IMPRINT",EDGE,{"disambiguationData":[TD([[subQ2,1.0]])],"derivedFrom":subQ1}),1.0]])]});}
            var Q39;
            {var subQ0=sQuery(id+"F1.wireOp",EDGE,"E13");var subQ1=sQuery(id+"F1.wireOp",EDGE,"E8.2.1");var subQ2=makeQuery(id+"F1.imprint","INTERSECT",VERTEX,{"derivedFrom":[subQ1,subQ0]});Q39=makeQuery(id+"F1.imprint","IMPRINT",FACE,{"disambiguationData":[TD([[makeQuery(id+"F1.imprint","IMPRINT",EDGE,{"disambiguationData":[TD([[subQ2,1.0]])],"derivedFrom":subQ1}),-1.0]])]});}
            var Q40;
            {var subQ0=sQuery(id+"F1.wireOp",EDGE,"E13");var subQ1=sQuery(id+"F1.wireOp",EDGE,"E8.3.1");var subQ2=makeQuery(id+"F1.imprint","INTERSECT",VERTEX,{"derivedFrom":[subQ1,subQ0]});Q40=makeQuery(id+"F1.imprint","IMPRINT",FACE,{"disambiguationData":[TD([[makeQuery(id+"F1.imprint","IMPRINT",EDGE,{"disambiguationData":[TD([[subQ2,-1.0]])],"derivedFrom":subQ1}),1.0]])]});}
            var Q41;
            {var subQ0=sQuery(id+"F1.wireOp",EDGE,"E14");var subQ1=sQuery(id+"F1.wireOp",EDGE,"E8.4.1");var subQ2=makeQuery(id+"F1.imprint","INTERSECT",VERTEX,{"derivedFrom":[subQ1,subQ0]});Q41=makeQuery(id+"F1.imprint","IMPRINT",FACE,{"disambiguationData":[TD([[makeQuery(id+"F1.imprint","IMPRINT",EDGE,{"disambiguationData":[TD([[subQ2,-1.0]])],"derivedFrom":subQ1}),1.0]])]});}
            var Q42;
            {var subQ0=sQuery(id+"F1.wireOp",EDGE,"E14");var subQ1=sQuery(id+"F1.wireOp",EDGE,"E8.3.1");var subQ2=makeQuery(id+"F1.imprint","INTERSECT",VERTEX,{"derivedFrom":[subQ1,subQ0]});Q42=makeQuery(id+"F1.imprint","IMPRINT",FACE,{"disambiguationData":[TD([[makeQuery(id+"F1.imprint","IMPRINT",EDGE,{"disambiguationData":[TD([[subQ2,1.0]])],"derivedFrom":subQ1}),1.0]])]});}
            var Q43;
            {var subQ0=sQuery(id+"F1.wireOp",EDGE,"E14");var subQ1=sQuery(id+"F1.wireOp",EDGE,"E8.3.1");var subQ2=makeQuery(id+"F1.imprint","INTERSECT",VERTEX,{"derivedFrom":[subQ1,subQ0]});Q43=makeQuery(id+"F1.imprint","IMPRINT",FACE,{"disambiguationData":[TD([[makeQuery(id+"F1.imprint","IMPRINT",EDGE,{"disambiguationData":[TD([[subQ2,1.0]])],"derivedFrom":subQ1}),-1.0]])]});}
            var Q44;
            {var subQ0=sQuery(id+"F1.wireOp",EDGE,"E15");var subQ1=sQuery(id+"F1.wireOp",EDGE,"E8.5.1");var subQ2=makeQuery(id+"F1.imprint","INTERSECT",VERTEX,{"derivedFrom":[subQ1,subQ0]});Q44=makeQuery(id+"F1.imprint","IMPRINT",FACE,{"disambiguationData":[TD([[makeQuery(id+"F1.imprint","IMPRINT",EDGE,{"disambiguationData":[TD([[subQ2,-1.0]])],"derivedFrom":subQ1}),1.0]])]});}
            var Q45;
            {var subQ0=sQuery(id+"F1.wireOp",EDGE,"E15");var subQ1=sQuery(id+"F1.wireOp",EDGE,"E8.4.1");var subQ2=makeQuery(id+"F1.imprint","INTERSECT",VERTEX,{"derivedFrom":[subQ1,subQ0]});Q45=makeQuery(id+"F1.imprint","IMPRINT",FACE,{"disambiguationData":[TD([[makeQuery(id+"F1.imprint","IMPRINT",EDGE,{"disambiguationData":[TD([[subQ2,1.0]])],"derivedFrom":subQ1}),1.0]])]});}
            var Q46;
            {var subQ0=sQuery(id+"F1.wireOp",EDGE,"E15");var subQ1=sQuery(id+"F1.wireOp",EDGE,"E8.4.1");var subQ2=makeQuery(id+"F1.imprint","INTERSECT",VERTEX,{"derivedFrom":[subQ1,subQ0]});Q46=makeQuery(id+"F1.imprint","IMPRINT",FACE,{"disambiguationData":[TD([[makeQuery(id+"F1.imprint","IMPRINT",EDGE,{"disambiguationData":[TD([[subQ2,1.0]])],"derivedFrom":subQ1}),-1.0]])]});}
            var Q47;
            {var subQ0=sQuery(id+"F1.wireOp",EDGE,"E27");Q47=makeQuery(id+"F1.imprint","IMPRINT",FACE,{"disambiguationData":[TD([[makeQuery(id+"F1.imprint","IMPRINT",EDGE,{"derivedFrom":subQ0}),1.0]])]});}
            var Q48;
            {var subQ0=sQuery(id+"F1.wireOp",EDGE,"E26");Q48=makeQuery(id+"F1.imprint","IMPRINT",FACE,{"disambiguationData":[TD([[makeQuery(id+"F1.imprint","IMPRINT",EDGE,{"derivedFrom":subQ0}),1.0]])]});}
            var Q49;
            {var subQ0=sQuery(id+"F1.wireOp",EDGE,"E25");Q49=makeQuery(id+"F1.imprint","IMPRINT",FACE,{"disambiguationData":[TD([[makeQuery(id+"F1.imprint","IMPRINT",EDGE,{"derivedFrom":subQ0}),1.0]])]});}
            var Q50;
            {var subQ0=sQuery(id+"F1.wireOp",EDGE,"E23");Q50=makeQuery(id+"F1.imprint","IMPRINT",FACE,{"disambiguationData":[TD([[makeQuery(id+"F1.imprint","IMPRINT",EDGE,{"derivedFrom":subQ0}),1.0]])]});}
            var Q51;
            {var subQ0=sQuery(id+"F1.wireOp",EDGE,"E24");Q51=makeQuery(id+"F1.imprint","IMPRINT",FACE,{"disambiguationData":[TD([[makeQuery(id+"F1.imprint","IMPRINT",EDGE,{"derivedFrom":subQ0}),1.0]])]});}
            extrude(context, id + "F2", {"entities" : qUnion([Q0, Q1, Q2, Q3, Q4, Q5, Q6, Q7, Q8, Q9, Q10, Q11, Q12, Q13, Q14, Q15, Q16, Q17, Q18, Q19, Q20, Q21, Q22, Q23, Q24, Q25, Q26, Q27, Q28, Q29, Q30, Q31, Q32, Q33, Q34, Q35, Q36, Q37, Q38, Q39, Q40, Q41, Q42, Q43, Q44, Q45, Q46, Q47, Q48, Q49, Q50, Q51]), "depth" : getVariable(context, 'clipHeight'), "offsetDistance" : 25 * mm});
        }
        {
            var Q0;
            {var subQ0=sQuery(id+"F1.wireOp",EDGE,"E9");var subQ1=sQuery(id+"F1.wireOp",EDGE,"E6");var subQ2=makeQuery(id+"F1.imprint","INTERSECT",VERTEX,{"derivedFrom":[subQ1,subQ0]});Q0=makeQuery(id+"F1.imprint","IMPRINT",FACE,{"disambiguationData":[TD([[makeQuery(id+"F1.imprint","IMPRINT",EDGE,{"disambiguationData":[TD([[subQ2,-1.0]])],"derivedFrom":subQ1}),-1.0]])]});}
            var Q1;
            {var subQ3=sQuery(id+"F1.wireOp",EDGE,"E12");var subQ5=sQuery(id+"F1.wireOp",EDGE,"E8.2.1");var subQ6=makeQuery(id+"F1.imprint","INTERSECT",VERTEX,{"derivedFrom":[subQ5,subQ3]});Q1=makeQuery(id+"F1.imprint","IMPRINT",FACE,{"disambiguationData":[TD([[makeQuery(id+"F1.imprint","IMPRINT",EDGE,{"disambiguationData":[TD([[subQ6,-1.0]])],"derivedFrom":subQ5}),-1.0]])]});}
            var Q2;
            {var subQ0=sQuery(id+"F1.wireOp",EDGE,"E10");Q2=makeQuery(id+"F1.imprint","IMPRINT",FACE,{"disambiguationData":[TD([[makeQuery(id+"F1.imprint","IMPRINT",EDGE,{"derivedFrom":subQ0}),1.0]])]});}
            var Q3;
            {var subQ0=sQuery(id+"F1.wireOp",EDGE,"E13");var subQ1=sQuery(id+"F1.wireOp",EDGE,"E8.2.1");var subQ2=makeQuery(id+"F1.imprint","INTERSECT",VERTEX,{"derivedFrom":[subQ1,subQ0]});Q3=makeQuery(id+"F1.imprint","IMPRINT",FACE,{"disambiguationData":[TD([[makeQuery(id+"F1.imprint","IMPRINT",EDGE,{"disambiguationData":[TD([[subQ2,1.0]])],"derivedFrom":subQ1}),-1.0]])]});}
            var Q4;
            {var subQ0=sQuery(id+"F1.wireOp",EDGE,"E14");var subQ1=sQuery(id+"F1.wireOp",EDGE,"E8.3.1");var subQ2=makeQuery(id+"F1.imprint","INTERSECT",VERTEX,{"derivedFrom":[subQ1,subQ0]});Q4=makeQuery(id+"F1.imprint","IMPRINT",FACE,{"disambiguationData":[TD([[makeQuery(id+"F1.imprint","IMPRINT",EDGE,{"disambiguationData":[TD([[subQ2,1.0]])],"derivedFrom":subQ1}),-1.0]])]});}
            var Q5;
            {var subQ0=sQuery(id+"F1.wireOp",EDGE,"E9");var subQ5=sQuery(id+"F1.wireOp",EDGE,"E8.5.1");var subQ6=makeQuery(id+"F1.imprint","INTERSECT",VERTEX,{"derivedFrom":[subQ5,subQ0]});Q5=makeQuery(id+"F1.imprint","IMPRINT",FACE,{"disambiguationData":[TD([[makeQuery(id+"F1.imprint","IMPRINT",EDGE,{"disambiguationData":[TD([[subQ6,1.0]])],"derivedFrom":subQ5}),-1.0]])]});}
            var Q6;
            {var subQ3=sQuery(id+"F1.wireOp",EDGE,"E21");var subQ5=sQuery(id+"F1.wireOp",EDGE,"E8.2.1");var subQ7=makeQuery(id+"F1.imprint","INTERSECT",VERTEX,{"derivedFrom":[subQ5,subQ3]});Q6=makeQuery(id+"F1.imprint","IMPRINT",FACE,{"disambiguationData":[TD([[makeQuery(id+"F1.imprint","IMPRINT",EDGE,{"disambiguationData":[TD([[subQ7,-1.0]])],"derivedFrom":subQ5}),-1.0]])]});}
            var Q7;
            {var subQ0=sQuery(id+"F1.wireOp",EDGE,"E9");var subQ1=sQuery(id+"F1.wireOp",EDGE,"E8.2.1");var subQ2=makeQuery(id+"F1.imprint","INTERSECT",VERTEX,{"derivedFrom":[subQ1,subQ0]});Q7=makeQuery(id+"F1.imprint","IMPRINT",FACE,{"disambiguationData":[TD([[makeQuery(id+"F1.imprint","IMPRINT",EDGE,{"disambiguationData":[TD([[subQ2,-1.0]])],"derivedFrom":subQ1}),-1.0]])]});}
            var Q8;
            {var subQ0=sQuery(id+"F1.wireOp",EDGE,"E9");var subQ1=sQuery(id+"F1.wireOp",EDGE,"E8.3.1");var subQ2=makeQuery(id+"F1.imprint","INTERSECT",VERTEX,{"derivedFrom":[subQ1,subQ0]});Q8=makeQuery(id+"F1.imprint","IMPRINT",FACE,{"disambiguationData":[TD([[makeQuery(id+"F1.imprint","IMPRINT",EDGE,{"disambiguationData":[TD([[subQ2,-1.0]])],"derivedFrom":subQ1}),-1.0]])]});}
            extrude(context, id + "F3", {"entities" : qUnion([Q0, Q1, Q2, Q3, Q4, Q5, Q6, Q7, Q8]), "depth" : 2.5 * mm, "offsetDistance" : 25 * mm});
        }
        {
            var Q0;
            Q0=makeQuery(id+"F2.opExtrude","SWEPT_BODY",BODY,{"disambiguationData":[OSD([sQuery(id+"F1.wireOp",EDGE,"E0"),sQuery(id+"F1.wireOp",EDGE,"E3"),sQuery(id+"F1.wireOp",EDGE,"E4.MirrorCS"),sQuery(id+"F1.wireOp",EDGE,"E6")])]});
            var Q1;
            Q1=makeQuery(id+"F2.opExtrude","SWEPT_BODY",BODY,{"disambiguationData":[OSD([sQuery(id+"F1.wireOp",EDGE,"E8.1.1"),sQuery(id+"F1.wireOp",EDGE,"E8.1.3"),sQuery(id+"F1.wireOp",EDGE,"E8.1.6"),sQuery(id+"F1.wireOp",EDGE,"E8.1.7")])]});
            var Q2;
            Q2=makeQuery(id+"F3.opExtrude","SWEPT_BODY",BODY,{"disambiguationData":[OSD([sQuery(id+"F1.wireOp",EDGE,"E6"),sQuery(id+"F1.wireOp",EDGE,"E8.1.1"),sQuery(id+"F1.wireOp",EDGE,"E9"),sQuery(id+"F1.wireOp",EDGE,"E11")])]});
            var Q3;
            Q3=makeQuery(id+"F3.opExtrude","SWEPT_BODY",BODY,{"disambiguationData":[OSD([sQuery(id+"F1.wireOp",EDGE,"E8.1.1"),sQuery(id+"F1.wireOp",EDGE,"E8.2.1"),sQuery(id+"F1.wireOp",EDGE,"E8.3.1"),sQuery(id+"F1.wireOp",EDGE,"E8.4.1"),sQuery(id+"F1.wireOp",EDGE,"E10"),sQuery(id+"F1.wireOp",EDGE,"E12"),sQuery(id+"F1.wireOp",EDGE,"E13"),sQuery(id+"F1.wireOp",EDGE,"E14")])]});
            var Q4;
            Q4=makeQuery(id+"F2.opExtrude","SWEPT_BODY",BODY,{"disambiguationData":[OSD([sQuery(id+"F1.wireOp",EDGE,"E8.2.1"),sQuery(id+"F1.wireOp",EDGE,"E8.2.3"),sQuery(id+"F1.wireOp",EDGE,"E8.2.6"),sQuery(id+"F1.wireOp",EDGE,"E8.2.7")])]});
            var Q5;
            Q5=makeQuery(id+"F2.opExtrude","SWEPT_BODY",BODY,{"disambiguationData":[OSD([sQuery(id+"F1.wireOp",EDGE,"E8.3.1"),sQuery(id+"F1.wireOp",EDGE,"E8.3.3"),sQuery(id+"F1.wireOp",EDGE,"E8.3.6"),sQuery(id+"F1.wireOp",EDGE,"E8.3.7")])]});
            var Q6;
            Q6=makeQuery(id+"F3.opExtrude","SWEPT_BODY",BODY,{"disambiguationData":[OSD([sQuery(id+"F1.wireOp",EDGE,"E8.4.1"),sQuery(id+"F1.wireOp",EDGE,"E8.5.1"),sQuery(id+"F1.wireOp",EDGE,"E9"),sQuery(id+"F1.wireOp",EDGE,"E15")])]});
            var Q7;
            Q7=makeQuery(id+"F2.opExtrude","SWEPT_BODY",BODY,{"disambiguationData":[OSD([sQuery(id+"F1.wireOp",EDGE,"E8.4.1"),sQuery(id+"F1.wireOp",EDGE,"E8.4.3"),sQuery(id+"F1.wireOp",EDGE,"E8.4.6"),sQuery(id+"F1.wireOp",EDGE,"E8.4.7")])]});
            var Q8;
            Q8=makeQuery(id+"F2.opExtrude","SWEPT_BODY",BODY,{"disambiguationData":[OSD([sQuery(id+"F1.wireOp",EDGE,"E8.5.1"),sQuery(id+"F1.wireOp",EDGE,"E8.5.3"),sQuery(id+"F1.wireOp",EDGE,"E8.5.6"),sQuery(id+"F1.wireOp",EDGE,"E8.5.7")])]});
            booleanBodies(context, id + "F4", {"operationType" : BooleanOperationType.UNION, "tools" : qUnion([Q0, Q1, Q2, Q3, Q4, Q5, Q6, Q7, Q8])});
        }
        {
            var Q0;
            Q0=makeQuery(id+"F2.opExtrude","SWEPT_EDGE",EDGE,{"disambiguationData":[OSD([sQuery(id+"F1.wireOp",EDGE,"E0"),sQuery(id+"F1.wireOp",EDGE,"E3")])]});
            var Q1;
            Q1=makeQuery(id+"F2.opExtrude","SWEPT_EDGE",EDGE,{"disambiguationData":[OSD([sQuery(id+"F1.wireOp",EDGE,"E0"),sQuery(id+"F1.wireOp",EDGE,"E4.MirrorCS")])]});
            var Q2;
            Q2=makeQuery(id+"F2.opExtrude","SWEPT_EDGE",EDGE,{"disambiguationData":[OSD([sQuery(id+"F1.wireOp",EDGE,"E8.1.3"),sQuery(id+"F1.wireOp",EDGE,"E8.1.7")])]});
            var Q3;
            Q3=makeQuery(id+"F2.opExtrude","SWEPT_EDGE",EDGE,{"disambiguationData":[OSD([sQuery(id+"F1.wireOp",EDGE,"E8.2.3"),sQuery(id+"F1.wireOp",EDGE,"E8.2.7")])]});
            var Q4;
            Q4=makeQuery(id+"F2.opExtrude","SWEPT_EDGE",EDGE,{"disambiguationData":[OSD([sQuery(id+"F1.wireOp",EDGE,"E8.3.3"),sQuery(id+"F1.wireOp",EDGE,"E8.3.7")])]});
            var Q5;
            Q5=makeQuery(id+"F2.opExtrude","SWEPT_EDGE",EDGE,{"disambiguationData":[OSD([sQuery(id+"F1.wireOp",EDGE,"E8.4.3"),sQuery(id+"F1.wireOp",EDGE,"E8.4.7")])]});
            var Q6;
            Q6=makeQuery(id+"F2.opExtrude","SWEPT_EDGE",EDGE,{"disambiguationData":[OSD([sQuery(id+"F1.wireOp",EDGE,"E8.5.3"),sQuery(id+"F1.wireOp",EDGE,"E8.5.7")])]});
            var Q7;
            Q7=makeQuery(id+"F2.opExtrude","SWEPT_EDGE",EDGE,{"disambiguationData":[OSD([sQuery(id+"F1.wireOp",EDGE,"E8.5.3"),sQuery(id+"F1.wireOp",EDGE,"E8.5.6")])]});
            var Q8;
            Q8=makeQuery(id+"F2.opExtrude","SWEPT_EDGE",EDGE,{"disambiguationData":[OSD([sQuery(id+"F1.wireOp",EDGE,"E8.4.3"),sQuery(id+"F1.wireOp",EDGE,"E8.4.6")])]});
            var Q9;
            Q9=makeQuery(id+"F2.opExtrude","SWEPT_EDGE",EDGE,{"disambiguationData":[OSD([sQuery(id+"F1.wireOp",EDGE,"E8.3.3"),sQuery(id+"F1.wireOp",EDGE,"E8.3.6")])]});
            var Q10;
            Q10=makeQuery(id+"F2.opExtrude","SWEPT_EDGE",EDGE,{"disambiguationData":[OSD([sQuery(id+"F1.wireOp",EDGE,"E8.2.3"),sQuery(id+"F1.wireOp",EDGE,"E8.2.6")])]});
            var Q11;
            Q11=makeQuery(id+"F2.opExtrude","SWEPT_EDGE",EDGE,{"disambiguationData":[OSD([sQuery(id+"F1.wireOp",EDGE,"E8.1.3"),sQuery(id+"F1.wireOp",EDGE,"E8.1.6")])]});
            fillet(context, id + "F5", {"entities" : qUnion([Q0, Q1, Q2, Q3, Q4, Q5, Q6, Q7, Q8, Q9, Q10, Q11]), "radius" : 1 * mm, "tangentPropagation" : true, "allowEdgeOverflow" : false});
        }
        {
            var Q0;
            Q0=qCreatedBy(makeId("Right.planeOp"),FACE);
            var sketch = newSketch(context, id + "F6", { "sketchPlane" : qUnion([Q0])});
            skLineSegment(sketch, "E28", {"start": v(83.1, 0) * mm, "end": v(83.1, 104.2) * mm, "construction": true});
            skSolve(sketch);
        }
        {
            var Q0;
            Q0=makeQuery(id+"F2.opExtrude","SWEPT_BODY",BODY,{"disambiguationData":[OSD([sQuery(id+"F1.wireOp",EDGE,"E0"),sQuery(id+"F1.wireOp",EDGE,"E3"),sQuery(id+"F1.wireOp",EDGE,"E4.MirrorCS"),sQuery(id+"F1.wireOp",EDGE,"E6")])]});
            var Q1;
            Q1=sQuery(id+"F6.wireOp",EDGE,"E28");
            var Q2;
            Q2=sQuery(id+"F6.wireOp",EDGE,"E28");
            transform(context, id + "F7", {"entities" : qUnion([Q0]), "transformType" : TransformType.ROTATION, "transformAxis" : qUnion([Q2]), "angle" : 37.5 * degree, "oppositeDirection" : true, "makeCopy" : false});
        }
        {
            var Q0;
            Q0=qCreatedBy(makeId("Right.planeOp"),FACE);
            var sketch = newSketch(context, id + "F8", { "sketchPlane" : qUnion([Q0])});
            skLineSegment(sketch, "E29", {"start": v(0, 0) * mm, "end": v(-22, 0) * mm, "construction": true});
            skLineSegment(sketch, "E30", {"start": v(-22, 0) * mm, "end": v(-22, 2.5) * mm, "construction": true});
            skArc(sketch, "E31", {"start": v(-22, 2.5) * mm, "mid": v(-25.5, 4.56) * mm, "end": v(-29, 2.5) * mm});
            skLineSegment(sketch, "E32", {"start": v(-29, 2.5) * mm, "end": v(-22, 2.5) * mm});
            skSolve(sketch);
        }
        {
            var Q0;
            Q0 = qSketchRegion(id + "F8", true);
            extrude(context, id + "F9", {"entities" : qUnion([Q0]), "operationType" : NewBodyOperationType.ADD, "endBound" : BoundingType.SYMMETRIC, "depth" : 25 * mm, "offsetDistance" : 25 * mm});
        }
        {
            var Q0;
            Q0=makeQuery(id+"F9.opExtrude","CAP_EDGE",EDGE,{"disambiguationData":[OSD([sQuery(id+"F8.wireOp",EDGE,"E31")])],"isStart":false});
            var Q1;
            Q1=makeQuery(id+"F9.opExtrude","CAP_EDGE",EDGE,{"disambiguationData":[OSD([sQuery(id+"F8.wireOp",EDGE,"E31")])],"isStart":true});
            fillet(context, id + "F10", {"entities" : qUnion([Q0, Q1]), "radius" : 3 * mm, "tangentPropagation" : true, "allowEdgeOverflow" : false});
        }
        {
            var Q0;
            {var subQ0=sQuery(id+"F1.wireOp",EDGE,"E10");var subQ1=sQuery(id+"F1.wireOp",EDGE,"E9");var subQ2=sQuery(id+"F1.wireOp",EDGE,"E8.1.1");Q0=makeQuery(id+"F4.opBoolean","MERGE",EDGE,{"derivedFrom":[makeQuery(id+"F3.opExtrude","SWEPT_EDGE",EDGE,{"disambiguationData":[OSD([subQ2,subQ1,subQ0]),OD(0.0)]}),makeQuery(id+"F3.opExtrude","SWEPT_EDGE",EDGE,{"disambiguationData":[OSD([subQ2,subQ1,subQ0]),OD(1.0)]})]});}
            var Q1;
            {var subQ0=sQuery(id+"F1.wireOp",EDGE,"E10");var subQ1=sQuery(id+"F1.wireOp",EDGE,"E9");var subQ2=sQuery(id+"F1.wireOp",EDGE,"E8.4.1");Q1=makeQuery(id+"F4.opBoolean","MERGE",EDGE,{"derivedFrom":[makeQuery(id+"F3.opExtrude","SWEPT_EDGE",EDGE,{"disambiguationData":[OSD([subQ2,subQ1,subQ0]),OD(0.0)]}),makeQuery(id+"F3.opExtrude","SWEPT_EDGE",EDGE,{"disambiguationData":[OSD([subQ2,subQ1,subQ0]),OD(1.0)]})]});}
            fillet(context, id + "F11", {"entities" : qUnion([Q0, Q1]), "radius" : 10 * mm, "tangentPropagation" : true, "allowEdgeOverflow" : false});
        }
        {
            var Q0;
            Q0=makeQuery(id+"F2.opExtrude","SWEPT_EDGE",EDGE,{"disambiguationData":[OSD([sQuery(id+"F1.wireOp",EDGE,"E8.1.1"),sQuery(id+"F1.wireOp",EDGE,"E21")])]});
            var Q1;
            Q1=makeQuery(id+"F2.opExtrude","SWEPT_EDGE",EDGE,{"disambiguationData":[OSD([sQuery(id+"F1.wireOp",EDGE,"E8.2.1"),sQuery(id+"F1.wireOp",EDGE,"E21")])]});
            var Q2;
            Q2=makeQuery(id+"F2.opExtrude","SWEPT_EDGE",EDGE,{"disambiguationData":[OSD([sQuery(id+"F1.wireOp",EDGE,"E8.1.1"),sQuery(id+"F1.wireOp",EDGE,"E22")])]});
            var Q3;
            Q3=makeQuery(id+"F2.opExtrude","SWEPT_EDGE",EDGE,{"disambiguationData":[OSD([sQuery(id+"F1.wireOp",EDGE,"E6"),sQuery(id+"F1.wireOp",EDGE,"E22")])]});
            var Q4;
            Q4=makeQuery(id+"F2.opExtrude","SWEPT_EDGE",EDGE,{"disambiguationData":[OSD([sQuery(id+"F1.wireOp",EDGE,"E8.2.1"),sQuery(id+"F1.wireOp",EDGE,"E20")])]});
            var Q5;
            Q5=makeQuery(id+"F2.opExtrude","SWEPT_EDGE",EDGE,{"disambiguationData":[OSD([sQuery(id+"F1.wireOp",EDGE,"E8.3.1"),sQuery(id+"F1.wireOp",EDGE,"E20")])]});
            var Q6;
            Q6=makeQuery(id+"F2.opExtrude","SWEPT_EDGE",EDGE,{"disambiguationData":[OSD([sQuery(id+"F1.wireOp",EDGE,"E8.3.1"),sQuery(id+"F1.wireOp",EDGE,"E19")])]});
            var Q7;
            Q7=makeQuery(id+"F2.opExtrude","SWEPT_EDGE",EDGE,{"disambiguationData":[OSD([sQuery(id+"F1.wireOp",EDGE,"E8.4.1"),sQuery(id+"F1.wireOp",EDGE,"E19")])]});
            var Q8;
            Q8=makeQuery(id+"F2.opExtrude","SWEPT_EDGE",EDGE,{"disambiguationData":[OSD([sQuery(id+"F1.wireOp",EDGE,"E8.4.1"),sQuery(id+"F1.wireOp",EDGE,"E18")])]});
            var Q9;
            Q9=makeQuery(id+"F2.opExtrude","SWEPT_EDGE",EDGE,{"disambiguationData":[OSD([sQuery(id+"F1.wireOp",EDGE,"E8.5.1"),sQuery(id+"F1.wireOp",EDGE,"E18")])]});
            fillet(context, id + "F12", {"entities" : qUnion([Q0, Q1, Q2, Q3, Q4, Q5, Q6, Q7, Q8, Q9]), "radius" : 1.5 * mm, "tangentPropagation" : true, "allowEdgeOverflow" : false});
        }
        {
            var Q0;
            Q0=makeQuery(id+"F3.opExtrude","CAP_EDGE",EDGE,{"disambiguationData":[OSD([sQuery(id+"F1.wireOp",EDGE,"E17")])],"isStart":true});
            var Q1;
            Q1=makeQuery(id+"F3.opExtrude","CAP_EDGE",EDGE,{"disambiguationData":[OSD([sQuery(id+"F1.wireOp",EDGE,"E17")])],"isStart":false});
            fillet(context, id + "F13", {"entities" : qUnion([Q0, Q1]), "radius" : 1.25 * mm, "tangentPropagation" : true, "allowEdgeOverflow" : false});
        }
        {
            var Q0;
            Q0=makeQuery(id+"F5.opFillet","BLEND_EDGE",EDGE,{"blendedFrom":[makeQuery(id+"F2.opExtrude","SWEPT_EDGE",EDGE,{"disambiguationData":[OSD([sQuery(id+"F1.wireOp",EDGE,"E8.5.3"),sQuery(id+"F1.wireOp",EDGE,"E8.5.7")])]}),makeQuery(id+"F2.opExtrude","SWEPT_FACE",FACE,{"disambiguationData":[OSD([sQuery(id+"F1.wireOp",EDGE,"E23")])]})],"blendedInto":[makeQuery(id+"F2.opExtrude","SWEPT_FACE",FACE,{"disambiguationData":[OSD([sQuery(id+"F1.wireOp",EDGE,"E23")])]})]});
            var Q1;
            Q1=makeQuery(id+"F5.opFillet","BLEND_EDGE",EDGE,{"blendedFrom":[makeQuery(id+"F2.opExtrude","SWEPT_EDGE",EDGE,{"disambiguationData":[OSD([sQuery(id+"F1.wireOp",EDGE,"E8.4.3"),sQuery(id+"F1.wireOp",EDGE,"E8.4.6")])]}),makeQuery(id+"F2.opExtrude","SWEPT_FACE",FACE,{"disambiguationData":[OSD([sQuery(id+"F1.wireOp",EDGE,"E23")])]})],"blendedInto":[makeQuery(id+"F2.opExtrude","SWEPT_FACE",FACE,{"disambiguationData":[OSD([sQuery(id+"F1.wireOp",EDGE,"E23")])]})]});
            var Q2;
            Q2=makeQuery(id+"F5.opFillet","BLEND_EDGE",EDGE,{"blendedFrom":[makeQuery(id+"F2.opExtrude","SWEPT_EDGE",EDGE,{"disambiguationData":[OSD([sQuery(id+"F1.wireOp",EDGE,"E8.3.3"),sQuery(id+"F1.wireOp",EDGE,"E8.3.6")])]}),makeQuery(id+"F2.opExtrude","SWEPT_FACE",FACE,{"disambiguationData":[OSD([sQuery(id+"F1.wireOp",EDGE,"E24")])]})],"blendedInto":[makeQuery(id+"F2.opExtrude","SWEPT_FACE",FACE,{"disambiguationData":[OSD([sQuery(id+"F1.wireOp",EDGE,"E24")])]})]});
            var Q3;
            Q3=makeQuery(id+"F5.opFillet","BLEND_EDGE",EDGE,{"blendedFrom":[makeQuery(id+"F2.opExtrude","SWEPT_EDGE",EDGE,{"disambiguationData":[OSD([sQuery(id+"F1.wireOp",EDGE,"E8.3.3"),sQuery(id+"F1.wireOp",EDGE,"E8.3.7")])]}),makeQuery(id+"F2.opExtrude","SWEPT_FACE",FACE,{"disambiguationData":[OSD([sQuery(id+"F1.wireOp",EDGE,"E25")])]})],"blendedInto":[makeQuery(id+"F2.opExtrude","SWEPT_FACE",FACE,{"disambiguationData":[OSD([sQuery(id+"F1.wireOp",EDGE,"E25")])]})]});
            var Q4;
            Q4=makeQuery(id+"F5.opFillet","BLEND_EDGE",EDGE,{"blendedFrom":[makeQuery(id+"F2.opExtrude","SWEPT_EDGE",EDGE,{"disambiguationData":[OSD([sQuery(id+"F1.wireOp",EDGE,"E8.4.3"),sQuery(id+"F1.wireOp",EDGE,"E8.4.7")])]}),makeQuery(id+"F2.opExtrude","SWEPT_FACE",FACE,{"disambiguationData":[OSD([sQuery(id+"F1.wireOp",EDGE,"E24")])]})],"blendedInto":[makeQuery(id+"F2.opExtrude","SWEPT_FACE",FACE,{"disambiguationData":[OSD([sQuery(id+"F1.wireOp",EDGE,"E24")])]})]});
            var Q5;
            Q5=makeQuery(id+"F5.opFillet","BLEND_EDGE",EDGE,{"blendedFrom":[makeQuery(id+"F2.opExtrude","SWEPT_EDGE",EDGE,{"disambiguationData":[OSD([sQuery(id+"F1.wireOp",EDGE,"E8.2.3"),sQuery(id+"F1.wireOp",EDGE,"E8.2.6")])]}),makeQuery(id+"F2.opExtrude","SWEPT_FACE",FACE,{"disambiguationData":[OSD([sQuery(id+"F1.wireOp",EDGE,"E25")])]})],"blendedInto":[makeQuery(id+"F2.opExtrude","SWEPT_FACE",FACE,{"disambiguationData":[OSD([sQuery(id+"F1.wireOp",EDGE,"E25")])]})]});
            var Q6;
            Q6=makeQuery(id+"F5.opFillet","BLEND_EDGE",EDGE,{"blendedFrom":[makeQuery(id+"F2.opExtrude","SWEPT_EDGE",EDGE,{"disambiguationData":[OSD([sQuery(id+"F1.wireOp",EDGE,"E8.2.3"),sQuery(id+"F1.wireOp",EDGE,"E8.2.7")])]}),makeQuery(id+"F2.opExtrude","SWEPT_FACE",FACE,{"disambiguationData":[OSD([sQuery(id+"F1.wireOp",EDGE,"E26")])]})],"blendedInto":[makeQuery(id+"F2.opExtrude","SWEPT_FACE",FACE,{"disambiguationData":[OSD([sQuery(id+"F1.wireOp",EDGE,"E26")])]})]});
            var Q7;
            Q7=makeQuery(id+"F5.opFillet","BLEND_EDGE",EDGE,{"blendedFrom":[makeQuery(id+"F2.opExtrude","SWEPT_EDGE",EDGE,{"disambiguationData":[OSD([sQuery(id+"F1.wireOp",EDGE,"E8.1.3"),sQuery(id+"F1.wireOp",EDGE,"E8.1.6")])]}),makeQuery(id+"F2.opExtrude","SWEPT_FACE",FACE,{"disambiguationData":[OSD([sQuery(id+"F1.wireOp",EDGE,"E26")])]})],"blendedInto":[makeQuery(id+"F2.opExtrude","SWEPT_FACE",FACE,{"disambiguationData":[OSD([sQuery(id+"F1.wireOp",EDGE,"E26")])]})]});
            var Q8;
            Q8=makeQuery(id+"F5.opFillet","BLEND_EDGE",EDGE,{"blendedFrom":[makeQuery(id+"F2.opExtrude","SWEPT_EDGE",EDGE,{"disambiguationData":[OSD([sQuery(id+"F1.wireOp",EDGE,"E8.1.3"),sQuery(id+"F1.wireOp",EDGE,"E8.1.7")])]}),makeQuery(id+"F2.opExtrude","SWEPT_FACE",FACE,{"disambiguationData":[OSD([sQuery(id+"F1.wireOp",EDGE,"E27")])]})],"blendedInto":[makeQuery(id+"F2.opExtrude","SWEPT_FACE",FACE,{"disambiguationData":[OSD([sQuery(id+"F1.wireOp",EDGE,"E27")])]})]});
            var Q9;
            Q9=makeQuery(id+"F5.opFillet","BLEND_EDGE",EDGE,{"blendedFrom":[makeQuery(id+"F2.opExtrude","SWEPT_EDGE",EDGE,{"disambiguationData":[OSD([sQuery(id+"F1.wireOp",EDGE,"E0"),sQuery(id+"F1.wireOp",EDGE,"E4.MirrorCS")])]}),makeQuery(id+"F2.opExtrude","SWEPT_FACE",FACE,{"disambiguationData":[OSD([sQuery(id+"F1.wireOp",EDGE,"E27")])]})],"blendedInto":[makeQuery(id+"F2.opExtrude","SWEPT_FACE",FACE,{"disambiguationData":[OSD([sQuery(id+"F1.wireOp",EDGE,"E27")])]})]});
            fillet(context, id + "F14", {"entities" : qUnion([Q0, Q1, Q2, Q3, Q4, Q5, Q6, Q7, Q8, Q9]), "radius" : 1 * mm, "tangentPropagation" : true, "allowEdgeOverflow" : false});
        }
    });
